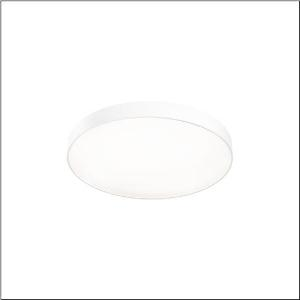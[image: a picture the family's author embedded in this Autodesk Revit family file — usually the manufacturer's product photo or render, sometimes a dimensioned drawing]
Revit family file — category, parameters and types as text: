
# Revit family: round_21_m_51mr36fm8321w
name_source: partatom
category: Lighting Fixtures
units: mm (PartAtom-declared; Revit-internal decimal feet)

## family parameters
Cut with Voids When Loaded = No
Host = Face
Light Source = No
Part Type = Normal
Room Calculation Point = No
Round Connector Dimension = Use Diameter
Shared = No

## types (1)
- --- (1 x LED, 7770 lm, 61.1 W, 3000K)
    Apparent Load = 61 VA
    CIE Flux Codes = 49 80 96 100 100
    Color Rendering = 80
    Color Temperature = 3000K
    Default Elevation = 1800 mm
    Description = Round 21 M, wall and ceiling luminaire, primary optical cover: cover, of PMMA, opal, light emission: direct distribution, primary light characteristic: symmetric, installation type: surface-mounted, suspended mounting, LED, rated luminous flux: 7.700lm, luminous efficacy: 127lm/W, light colour: 830, colour temperature: 3000K, with terminal, 3-pole, mains connection: 230V, AC, 50/60Hz, rated input power: 61W, housing, of aluminium, coated, white, diameter: 600mm, height: 62mm, protection rating (complete): IP40, insulation class (complete): insulation class I (protective earthing), certification: CE, impact resistance: IK04, permissible operating ambient temperature: -10..+35°C, packaging unit: 1 piece
    Height = 87 mm
    Lamp = 1 x LED
    Lamp Light Flux = 7770 lm
    Lamp Power = 61.1 W
    Lamp count = 1
    Length = 600 mm
    Luminous efficacy = 127 lm/W
    Manufacturer = Siteco
    ModVariant = No
    Model = 51MR36FM8321W
    Mounting Place = Ceiling
    Mounting Type = Surface mounted
    Number of Poles = 1
    OnlyDefault = Yes
    Power Factor = 1
    Product Name = Round 21 M
    Product group = wall and ceiling luminaire
    ProductGroupID = 302
    Protection Class = Protection class I
    Protection Degree = IP 40
    RLX_Detail_Level = 1
    RLX_Emergency_Light_Flux = 0 lm
    RLX_Emergency_Type = 0
    RLX_Emergency_Type_DB = No
    RlxData = <blob elided: 14337 chars, md5=0b67ad98>
    Socket = socket
    Standby Power = 0 W
    System Light Flux = 7770 lm
    System Power = 61 W
    Type Comments = factory setting: luminous flux: 100 % | (ON | ON | ON | ON) | 700 mA
    Type Image = l_1258330.jpg
    URL = http://relux.com
    VarID = @adj_028607
    Voltage = 0 V
    Weight = 0.00 kg
    Width = 0 mm  [stored 0 ft]

note: [stored X ft] marks values corroborated as IEEE doubles in the binary element streams (Revit-internal decimal feet)

## geometry (parser evidence)
native form markers: Sweep x12
no freeform markers — native parametric forms only
